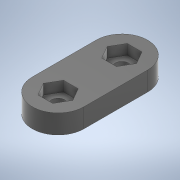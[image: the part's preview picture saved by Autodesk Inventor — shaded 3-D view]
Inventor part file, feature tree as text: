
AUTODESK INVENTOR PART (.ipt)
format: ipt  version: 2020 (Build 240168000, 168)  size: 299,520 bytes
history: native  units: mm
features: extrude x3, sketch x3
ambient origin geometry x8: Origin, YZ Plane, XZ Plane, XY Plane, X Axis, Y Axis, Z Axis, Center Point
bodies: Volumenkörper1 (feature_tree)
feature tree (6):
  extrude  "Extrusion1"  Depth=10.0mm
  extrude  "Extrusion2"  Depth=3.0mm TaperAngle=0.0deg
  extrude  "Extrusion3"  Depth=1.6mm TaperAngle=0.0deg
  sketch  "Skizze1"  dims[d0=2.1mm d1=10.0mm]
  sketch  "Skizze2"  dims[d2=3.0mm d3=3.0mm d4=0.0mm]
  sketch  "Skizze3"  dims[d5=4.0mm d6=1.6mm d7=0.0mm d8=3.0mm d9=1.5mm d10=0.0mm]
